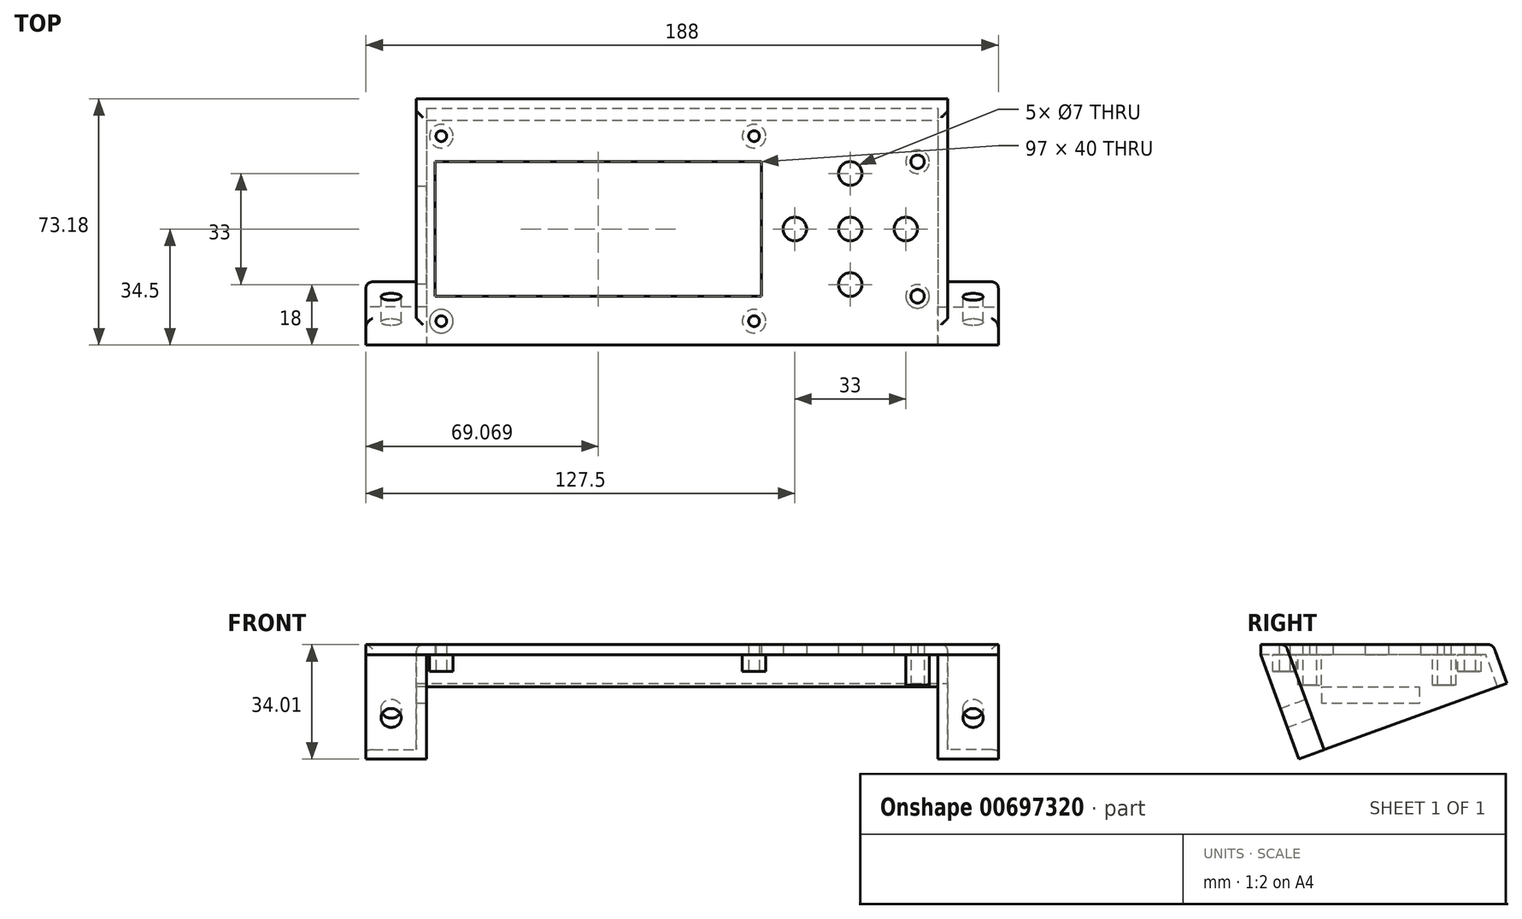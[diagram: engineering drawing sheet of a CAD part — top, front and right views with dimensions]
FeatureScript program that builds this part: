
annotation { "Feature Type Name" : "Feature", "Feature Type Description" : "" }
export const myFeature = defineFeature(function(context is Context, id is Id, definition is map)
    precondition{}
    {
        {
            var Q0;
            Q0=qCreatedBy(makeId("Top.planeOp"),FACE);
            var sketch = newSketch(context, id + "F0", { "sketchPlane" : qUnion([Q0])});
            skLineSegment(sketch, "E0.bottom", {"start": v(74, 29.5) * mm, "end": v(-74, 29.5) * mm});
            skLineSegment(sketch, "E0.top", {"start": v(74, -29.5) * mm, "end": v(-74, -29.5) * mm});
            skLineSegment(sketch, "E0.left", {"start": v(74, 29.5) * mm, "end": v(74, -29.5) * mm});
            skLineSegment(sketch, "E0.right", {"start": v(-74, 29.5) * mm, "end": v(-74, -29.5) * mm});
            skPoint(sketch, "E0.middle", {"position": v(0, 0) * mm});
            skCircle(sketch, "E1", {"center": v(30, 20) * mm, "radius": 2 * mm});
            skCircle(sketch, "E2.0.1.0", {"center": v(30, -20) * mm, "radius": 2 * mm});
            skCircle(sketch, "E2.1.0.0", {"center": v(70, 20) * mm, "radius": 2 * mm});
            skCircle(sketch, "E2.1.1.0", {"center": v(70, -20) * mm, "radius": 2 * mm});
            skLineSegment(sketch, "E2.direction1", {"start": v(30, 20) * mm, "end": v(70, 20) * mm, "construction": true});
            skLineSegment(sketch, "E2.direction2", {"start": v(30, 20) * mm, "end": v(30, -20) * mm, "construction": true});
            skCircle(sketch, "E3", {"center": v(-71.6, 27.6) * mm, "radius": 1.6 * mm});
            skCircle(sketch, "E4.0.1.0", {"center": v(-71.6, -27.4) * mm, "radius": 1.6 * mm});
            skCircle(sketch, "E4.1.0.0", {"center": v(21.4, 27.6) * mm, "radius": 1.6 * mm});
            skCircle(sketch, "E4.1.1.0", {"center": v(21.4, -27.4) * mm, "radius": 1.6 * mm});
            skLineSegment(sketch, "E4.direction1", {"start": v(-71.6, 27.6) * mm, "end": v(21.4, 27.6) * mm, "construction": true});
            skLineSegment(sketch, "E4.direction2", {"start": v(-71.6, 27.6) * mm, "end": v(-71.6, -27.4) * mm, "construction": true});
            skCircle(sketch, "E5", {"center": v(50, 0) * mm, "radius": 3.5 * mm});
            skCircle(sketch, "E6.1.0.0", {"center": v(66.5, 0) * mm, "radius": 3.5 * mm});
            skLineSegment(sketch, "E6.direction1", {"start": v(50, 0) * mm, "end": v(66.5, 0) * mm, "construction": true});
            skCircle(sketch, "E7.1.0.0", {"center": v(33.5, 0) * mm, "radius": 3.5 * mm});
            skLineSegment(sketch, "E7.direction1", {"start": v(50, 0) * mm, "end": v(33.5, 0) * mm, "construction": true});
            skCircle(sketch, "E8.0.1.0", {"center": v(50, 16.5) * mm, "radius": 3.5 * mm});
            skLineSegment(sketch, "E8.direction1", {"start": v(50, 0) * mm, "end": v(75.2, 0) * mm, "construction": true});
            skLineSegment(sketch, "E8.direction2", {"start": v(50, 0) * mm, "end": v(50, 16.5) * mm, "construction": true});
            skCircle(sketch, "E9.0.1.0", {"center": v(50, -16.5) * mm, "radius": 3.5 * mm});
            skLineSegment(sketch, "E9.direction2", {"start": v(50, 0) * mm, "end": v(50, -16.5) * mm, "construction": true});
            skLineSegment(sketch, "E10", {"start": v(21.4, -27.4) * mm, "end": v(-71.6, 27.6) * mm, "construction": true});
            skLineSegment(sketch, "E11", {"start": v(21.4, 27.6) * mm, "end": v(-71.6, -27.4) * mm, "construction": true});
            skPoint(sketch, "E12.middle", {"position": v(-24.93, 0) * mm});
            skLineSegment(sketch, "E13.bottom", {"start": v(23.57, 20) * mm, "end": v(-73.43, 20) * mm});
            skLineSegment(sketch, "E13.top", {"start": v(23.57, -20) * mm, "end": v(-73.43, -20) * mm});
            skLineSegment(sketch, "E13.left", {"start": v(23.57, 20) * mm, "end": v(23.57, -20) * mm});
            skLineSegment(sketch, "E13.right", {"start": v(-73.43, 20) * mm, "end": v(-73.43, -20) * mm});
            skSolve(sketch);
        }
        {
            var Q0;
            Q0=makeQuery(id+"F0.imprint","IMPRINT",FACE,{"disambiguationData":[TD([[makeQuery(id+"F0.imprint","IMPRINT",EDGE,{"derivedFrom":sQuery(id+"F0.wireOp",EDGE,"E0.bottom")}),1.0]])]});
            var Q1;
            Q1=makeQuery(id+"F0.imprint","IMPRINT",FACE,{"disambiguationData":[TD([[makeQuery(id+"F0.imprint","IMPRINT",EDGE,{"derivedFrom":sQuery(id+"F0.wireOp",EDGE,"E2.0.1.0")}),1.0]])]});
            var Q2;
            Q2=makeQuery(id+"F0.imprint","IMPRINT",FACE,{"disambiguationData":[TD([[makeQuery(id+"F0.imprint","IMPRINT",EDGE,{"derivedFrom":sQuery(id+"F0.wireOp",EDGE,"E1")}),1.0]])]});
            extrude(context, id + "F1", {"entities" : qUnion([Q0, Q1, Q2]), "depth" : 3 * mm, "offsetDistance" : 25 * mm});
        }
        {
            var Q0;
            Q0=makeQuery(id+"F1.opExtrude","CAP_FACE",FACE,{"disambiguationData":[OSD([sQuery(id+"F0.wireOp",EDGE,"E0.bottom"),sQuery(id+"F0.wireOp",EDGE,"E0.top"),sQuery(id+"F0.wireOp",EDGE,"E0.left"),sQuery(id+"F0.wireOp",EDGE,"E0.right"),sQuery(id+"F0.wireOp",EDGE,"E2.1.0.0"),sQuery(id+"F0.wireOp",EDGE,"E2.1.1.0"),sQuery(id+"F0.wireOp",EDGE,"E3"),sQuery(id+"F0.wireOp",EDGE,"E4.0.1.0"),sQuery(id+"F0.wireOp",EDGE,"E5"),sQuery(id+"F0.wireOp",EDGE,"E6.1.0.0"),sQuery(id+"F0.wireOp",EDGE,"E7.1.0.0"),sQuery(id+"F0.wireOp",EDGE,"E8.0.1.0"),sQuery(id+"F0.wireOp",EDGE,"E9.0.1.0"),sQuery(id+"F0.wireOp",EDGE,"E13.bottom"),sQuery(id+"F0.wireOp",EDGE,"E13.top"),sQuery(id+"F0.wireOp",EDGE,"E13.left"),sQuery(id+"F0.wireOp",EDGE,"E13.right")])],"isStart":true});
            var sketch = newSketch(context, id + "F2", { "sketchPlane" : qUnion([Q0])});
            skCircle(sketch, "E14", {"center": v(70, -20) * mm, "radius": 3.5 * mm});
            skCircle(sketch, "E15", {"center": v(70, 20) * mm, "radius": 3.5 * mm});
            skCircle(sketch, "E16", {"center": v(-71.6, -27.6) * mm, "radius": 3.5 * mm});
            skCircle(sketch, "E17", {"center": v(-71.6, 27.4) * mm, "radius": 3.5 * mm});
            skPoint(sketch, "E18.0", {"position": v(30, 20) * mm});
            skPoint(sketch, "E19.0", {"position": v(30, -20) * mm});
            skCircle(sketch, "E20.0", {"center": v(21.4, -27.6) * mm, "radius": 1.6 * mm});
            skCircle(sketch, "E20.1", {"center": v(21.4, 27.4) * mm, "radius": 1.6 * mm});
            skCircle(sketch, "E21", {"center": v(21.4, -27.6) * mm, "radius": 3.5 * mm});
            skCircle(sketch, "E22", {"center": v(21.4, 27.4) * mm, "radius": 3.5 * mm});
            skSolve(sketch);
        }
        {
            var Q0;
            Q0=makeQuery(id+"F2.imprint","IMPRINT",FACE,{"disambiguationData":[TD([[makeQuery(id+"F2.imprint","IMPRINT",EDGE,{"derivedFrom":sQuery(id+"F2.wireOp",EDGE,"E14")}),1.0]])]});
            var Q1;
            Q1=makeQuery(id+"F2.imprint","IMPRINT",FACE,{"disambiguationData":[TD([[makeQuery(id+"F2.imprint","IMPRINT",EDGE,{"derivedFrom":sQuery(id+"F2.wireOp",EDGE,"E15")}),1.0]])]});
            extrude(context, id + "F3", {"entities" : qUnion([Q0, Q1]), "operationType" : NewBodyOperationType.ADD, "depth" : 9 * mm, "offsetDistance" : 25 * mm});
        }
        {
            var Q0;
            Q0=makeQuery(id+"F2.imprint","IMPRINT",FACE,{"disambiguationData":[TD([[makeQuery(id+"F2.imprint","IMPRINT",EDGE,{"derivedFrom":makeQuery(id+"F1.opExtrude","CAP_EDGE",EDGE,{"disambiguationData":[OSD([sQuery(id+"F0.wireOp",EDGE,"E3")])],"isStart":true})}),1.0]])]});
            var Q1;
            {var subQ0=sQuery(id+"F2.wireOp",EDGE,"E16");var subQ1=makeQuery(id+"F1.opExtrude","CAP_EDGE",EDGE,{"disambiguationData":[OSD([sQuery(id+"F0.wireOp",EDGE,"E0.bottom")])],"isStart":true});var subQ2=makeQuery(id+"F2.imprint","INTERSECT",VERTEX,{"derivedFrom":[subQ1,subQ0]});Q1=makeQuery(id+"F2.imprint","IMPRINT",FACE,{"disambiguationData":[TD([[makeQuery(id+"F2.imprint","IMPRINT",EDGE,{"disambiguationData":[TD([[subQ2,1.0]])],"derivedFrom":subQ0}),1.0]])]});}
            var Q2;
            Q2=makeQuery(id+"F2.imprint","IMPRINT",FACE,{"disambiguationData":[TD([[makeQuery(id+"F2.imprint","IMPRINT",EDGE,{"derivedFrom":makeQuery(id+"F1.opExtrude","CAP_EDGE",EDGE,{"disambiguationData":[OSD([sQuery(id+"F0.wireOp",EDGE,"E4.0.1.0")])],"isStart":true})}),1.0]])]});
            var Q3;
            {var subQ0=sQuery(id+"F2.wireOp",EDGE,"E17");var subQ1=makeQuery(id+"F1.opExtrude","CAP_EDGE",EDGE,{"disambiguationData":[OSD([sQuery(id+"F0.wireOp",EDGE,"E0.top")])],"isStart":true});var subQ2=makeQuery(id+"F2.imprint","INTERSECT",VERTEX,{"derivedFrom":[subQ1,subQ0]});Q3=makeQuery(id+"F2.imprint","IMPRINT",FACE,{"disambiguationData":[TD([[makeQuery(id+"F2.imprint","IMPRINT",EDGE,{"disambiguationData":[TD([[subQ2,-1.0]])],"derivedFrom":subQ0}),1.0]])]});}
            var Q4;
            {var subQ0=sQuery(id+"F2.wireOp",EDGE,"E21");var subQ1=makeQuery(id+"F1.opExtrude","CAP_EDGE",EDGE,{"disambiguationData":[OSD([sQuery(id+"F0.wireOp",EDGE,"E0.bottom")])],"isStart":true});var subQ2=makeQuery(id+"F2.imprint","INTERSECT",VERTEX,{"disambiguationData":[OD(0.0)],"derivedFrom":[subQ1,subQ0]});Q4=makeQuery(id+"F2.imprint","IMPRINT",FACE,{"disambiguationData":[TD([[makeQuery(id+"F2.imprint","IMPRINT",EDGE,{"disambiguationData":[TD([[subQ2,1.0]])],"derivedFrom":subQ0}),1.0]])]});}
            var Q5;
            Q5=makeQuery(id+"F2.imprint","IMPRINT",FACE,{"disambiguationData":[TD([[makeQuery(id+"F2.imprint","IMPRINT",EDGE,{"derivedFrom":sQuery(id+"F2.wireOp",EDGE,"E20.0")}),1.0]])]});
            var Q6;
            Q6=makeQuery(id+"F2.imprint","IMPRINT",FACE,{"disambiguationData":[TD([[makeQuery(id+"F2.imprint","IMPRINT",EDGE,{"derivedFrom":sQuery(id+"F2.wireOp",EDGE,"E20.1")}),1.0]])]});
            var Q7;
            {var subQ0=sQuery(id+"F2.wireOp",EDGE,"E22");var subQ1=makeQuery(id+"F1.opExtrude","CAP_EDGE",EDGE,{"disambiguationData":[OSD([sQuery(id+"F0.wireOp",EDGE,"E0.top")])],"isStart":true});var subQ2=makeQuery(id+"F2.imprint","INTERSECT",VERTEX,{"disambiguationData":[OD(0.0)],"derivedFrom":[subQ1,subQ0]});Q7=makeQuery(id+"F2.imprint","IMPRINT",FACE,{"disambiguationData":[TD([[makeQuery(id+"F2.imprint","IMPRINT",EDGE,{"disambiguationData":[TD([[subQ2,-1.0]])],"derivedFrom":subQ0}),1.0]])]});}
            extrude(context, id + "F4", {"entities" : qUnion([Q0, Q1, Q2, Q3, Q4, Q5, Q6, Q7]), "operationType" : NewBodyOperationType.ADD, "depth" : 5 * mm, "offsetDistance" : 25 * mm});
        }
        {
            var Q0;
            Q0=makeQuery(id+"F1.opExtrude","SWEPT_FACE",FACE,{"disambiguationData":[OSD([sQuery(id+"F0.wireOp",EDGE,"E0.right")])]});
            extrude(context, id + "F5", {"entities" : qUnion([Q0]), "operationType" : NewBodyOperationType.ADD, "depth" : 5 * mm, "offsetDistance" : 25 * mm});
        }
        {
            var Q0;
            {var subQ0=sQuery(id+"F0.wireOp",EDGE,"E0.bottom");Q0=makeQuery(id+"F5.boolean.opBoolean","MERGE",FACE,{"derivedFrom":[makeQuery(id+"F1.opExtrude","SWEPT_FACE",FACE,{"disambiguationData":[OSD([subQ0])]}),makeQuery(id+"F5.opExtrude","SWEPT_FACE",FACE,{"disambiguationData":[OSD([subQ0,sQuery(id+"F0.wireOp",EDGE,"E0.right")])]})]});}
            extrude(context, id + "F6", {"entities" : qUnion([Q0]), "operationType" : NewBodyOperationType.ADD, "depth" : 5 * mm, "offsetDistance" : 25 * mm});
        }
        {
            var Q0;
            {var subQ0=sQuery(id+"F0.wireOp",EDGE,"E0.top");Q0=makeQuery(id+"F5.boolean.opBoolean","MERGE",FACE,{"derivedFrom":[makeQuery(id+"F1.opExtrude","SWEPT_FACE",FACE,{"disambiguationData":[OSD([subQ0])]}),makeQuery(id+"F5.opExtrude","SWEPT_FACE",FACE,{"disambiguationData":[OSD([subQ0,sQuery(id+"F0.wireOp",EDGE,"E0.right")])]})]});}
            extrude(context, id + "F7", {"entities" : qUnion([Q0]), "operationType" : NewBodyOperationType.ADD, "depth" : 5 * mm, "offsetDistance" : 25 * mm});
        }
        {
            var Q0;
            {var subQ0=sQuery(id+"F0.wireOp",EDGE,"E0.left");Q0=makeQuery(id+"F7.boolean.opBoolean","MERGE",FACE,{"derivedFrom":[makeQuery(id+"F6.boolean.opBoolean","MERGE",FACE,{"derivedFrom":[makeQuery(id+"F1.opExtrude","SWEPT_FACE",FACE,{"disambiguationData":[OSD([subQ0])]}),makeQuery(id+"F6.opExtrude","SWEPT_FACE",FACE,{"disambiguationData":[OSD([sQuery(id+"F0.wireOp",EDGE,"E0.bottom"),subQ0])]})]}),makeQuery(id+"F7.opExtrude","SWEPT_FACE",FACE,{"disambiguationData":[OSD([sQuery(id+"F0.wireOp",EDGE,"E0.top"),subQ0])]})]});}
            extrude(context, id + "F8", {"entities" : qUnion([Q0]), "operationType" : NewBodyOperationType.ADD, "depth" : 5 * mm, "offsetDistance" : 25 * mm});
        }
        {
            var Q0;
            Q0=makeQuery(id+"F8.opExtrude","CAP_FACE",FACE,{"disambiguationData":[OSD([sQuery(id+"F0.wireOp",EDGE,"E0.bottom"),sQuery(id+"F0.wireOp",EDGE,"E0.top"),sQuery(id+"F0.wireOp",EDGE,"E0.left")])],"isStart":false});
            var sketch = newSketch(context, id + "F9", { "sketchPlane" : qUnion([Q0])});
            skLineSegment(sketch, "E23", {"start": v(-34.5, 0) * mm, "end": v(-24.24, -28.2) * mm});
            skLineSegment(sketch, "E24", {"start": v(34.5, 3) * mm, "end": v(37.65, -5.66) * mm});
            skLineSegment(sketch, "E25", {"start": v(37.65, -5.66) * mm, "end": v(-24.24, -28.2) * mm});
            skSolve(sketch);
        }
        {
            var Q0;
            Q0 = qSketchRegion(id + "F9", true);
            var Q1;
            Q1=makeQuery(id+"F9.imprint","IMPRINT",FACE,{"disambiguationData":[TD([[makeQuery(id+"F9.imprint","IMPRINT",EDGE,{"derivedFrom":sQuery(id+"F9.wireOp",EDGE,"E23")}),1.0]])]});
            extrude(context, id + "F10", {"entities" : qUnion([Q0, Q1]), "operationType" : NewBodyOperationType.ADD, "oppositeDirection" : true, "depth" : 3 * mm, "offsetDistance" : 25 * mm});
        }
        {
            var Q0;
            {var subQ0=sQuery(id+"F0.wireOp",EDGE,"E0.right");var subQ1=sQuery(id+"F0.wireOp",EDGE,"E0.top");var subQ2=sQuery(id+"F0.wireOp",EDGE,"E0.bottom");Q0=makeQuery(id+"F7.boolean.opBoolean","MERGE",FACE,{"derivedFrom":[makeQuery(id+"F6.boolean.opBoolean","MERGE",FACE,{"derivedFrom":[makeQuery(id+"F5.opExtrude","CAP_FACE",FACE,{"disambiguationData":[OSD([subQ0])],"isStart":false}),makeQuery(id+"F6.opExtrude","SWEPT_FACE",FACE,{"disambiguationData":[OSD([subQ2,subQ0]),TDD([makeQuery(id+"F5.opExtrude","CAP_EDGE",EDGE,{"disambiguationData":[OSD([subQ2,subQ0])],"isStart":false})])]})]}),makeQuery(id+"F7.opExtrude","SWEPT_FACE",FACE,{"disambiguationData":[OSD([subQ1,subQ0]),TDD([makeQuery(id+"F5.opExtrude","CAP_EDGE",EDGE,{"disambiguationData":[OSD([subQ1,subQ0])],"isStart":false})])]})]});}
            var sketch = newSketch(context, id + "F11", { "sketchPlane" : qUnion([Q0])});
            skLineSegment(sketch, "E26.1.0", {"start": v(-34.5, 3) * mm, "end": v(-37.65, -5.66) * mm});
            skLineSegment(sketch, "E26.1.1", {"start": v(-37.65, -5.66) * mm, "end": v(24.24, -28.2) * mm});
            skLineSegment(sketch, "E26.1.2", {"start": v(24.24, -28.2) * mm, "end": v(34.5, 0) * mm});
            skLineSegment(sketch, "E26.1.3", {"start": v(34.5, 0) * mm, "end": v(-34.5, 0) * mm});
            skLineSegment(sketch, "E26.1.4", {"start": v(-34.5, 0) * mm, "end": v(-34.5, 3) * mm});
            skLineSegment(sketch, "E27.0", {"start": v(16.4, -9.5) * mm, "end": v(-12.6, -9.5) * mm});
            skLineSegment(sketch, "E28", {"start": v(-12.6, -9.5) * mm, "end": v(-12.6, -14.5) * mm});
            skLineSegment(sketch, "E29", {"start": v(-27.6, -9.32) * mm, "end": v(-27.6, -9.5) * mm});
            skLineSegment(sketch, "E30", {"start": v(-12.6, -14.5) * mm, "end": v(16.4, -14.5) * mm});
            skLineSegment(sketch, "E31", {"start": v(16.4, -14.5) * mm, "end": v(16.4, -9.5) * mm});
            skLineSegment(sketch, "E32.trimOffspring", {"start": v(-27.11, -9.5) * mm, "end": v(-27.6, -9.5) * mm});
            skSolve(sketch);
        }
        {
            var Q0;
            Q0=makeQuery(id+"F11.imprint","IMPRINT",FACE,{"disambiguationData":[TD([[makeQuery(id+"F11.imprint","IMPRINT",EDGE,{"derivedFrom":sQuery(id+"F11.wireOp",EDGE,"E26.1.0")}),1.0]])]});
            extrude(context, id + "F12", {"entities" : qUnion([Q0]), "operationType" : NewBodyOperationType.ADD, "oppositeDirection" : true, "depth" : 3 * mm, "offsetDistance" : 25 * mm});
        }
        {
            var Q0;
            Q0=makeQuery(id+"F10.opExtrude","CAP_FACE",FACE,{"disambiguationData":[OSD([sQuery(id+"F0.wireOp",EDGE,"E0.bottom"),sQuery(id+"F0.wireOp",EDGE,"E0.top"),sQuery(id+"F0.wireOp",EDGE,"E0.left"),sQuery(id+"F9.wireOp",EDGE,"E23"),sQuery(id+"F9.wireOp",EDGE,"E24"),sQuery(id+"F9.wireOp",EDGE,"E25")])],"isStart":false});
            var sketch = newSketch(context, id + "F13", { "sketchPlane" : qUnion([Q0])});
            skLineSegment(sketch, "E33", {"start": v(-34.83, -6.69) * mm, "end": v(-32.4, 0) * mm});
            skSolve(sketch);
        }
        {
            var Q0;
            Q0 = qSketchRegion(id + "F13", true);
            var Q1;
            {var subQ5=sQuery(id+"F13.wireOp",EDGE,"E33");Q1=makeQuery(id+"F13.imprint","IMPRINT",FACE,{"disambiguationData":[TD([[makeQuery(id+"F13.imprint","IMPRINT",EDGE,{"derivedFrom":subQ5}),1.0]])]});}
            extrude(context, id + "F14", {"entities" : qUnion([Q0, Q1]), "operationType" : NewBodyOperationType.ADD, "endBound" : BoundingType.UP_TO_NEXT, "depth" : 122 * mm, "offsetDistance" : 25 * mm});
        }
        {
            var Q0;
            {var subQ0=sQuery(id+"F0.wireOp",EDGE,"E0.right");var subQ1=sQuery(id+"F0.wireOp",EDGE,"E0.top");var subQ2=sQuery(id+"F0.wireOp",EDGE,"E0.bottom");Q0=makeQuery(id+"F12.boolean.opBoolean","MERGE",FACE,{"derivedFrom":[makeQuery(id+"F7.boolean.opBoolean","MERGE",FACE,{"derivedFrom":[makeQuery(id+"F6.boolean.opBoolean","MERGE",FACE,{"derivedFrom":[makeQuery(id+"F5.opExtrude","CAP_FACE",FACE,{"disambiguationData":[OSD([subQ0])],"isStart":false}),makeQuery(id+"F6.opExtrude","SWEPT_FACE",FACE,{"disambiguationData":[OSD([subQ2,subQ0]),TDD([makeQuery(id+"F5.opExtrude","CAP_EDGE",EDGE,{"disambiguationData":[OSD([subQ2,subQ0])],"isStart":false})])]})]}),makeQuery(id+"F7.opExtrude","SWEPT_FACE",FACE,{"disambiguationData":[OSD([subQ1,subQ0]),TDD([makeQuery(id+"F5.opExtrude","CAP_EDGE",EDGE,{"disambiguationData":[OSD([subQ1,subQ0])],"isStart":false})])]})]}),makeQuery(id+"F12.opExtrude","CAP_FACE",FACE,{"disambiguationData":[OSD([sQuery(id+"F11.wireOp",EDGE,"E26.1.0"),sQuery(id+"F11.wireOp",EDGE,"E26.1.1"),sQuery(id+"F11.wireOp",EDGE,"E26.1.2"),sQuery(id+"F11.wireOp",EDGE,"E26.1.3"),sQuery(id+"F11.wireOp",EDGE,"E26.1.4")])],"isStart":true})]});}
            var sketch = newSketch(context, id + "F15", { "sketchPlane" : qUnion([Q0])});
            skLineSegment(sketch, "E34", {"start": v(16.72, -25.45) * mm, "end": v(27.08, 3) * mm});
            skSolve(sketch);
        }
        {
            var Q0;
            {var subQ0=sQuery(id+"F0.wireOp",EDGE,"E0.left");var subQ1=sQuery(id+"F0.wireOp",EDGE,"E0.top");var subQ2=sQuery(id+"F0.wireOp",EDGE,"E0.bottom");Q0=makeQuery(id+"F10.boolean.opBoolean","MERGE",FACE,{"derivedFrom":[makeQuery(id+"F8.opExtrude","CAP_FACE",FACE,{"disambiguationData":[OSD([subQ2,subQ1,subQ0])],"isStart":false}),makeQuery(id+"F10.opExtrude","CAP_FACE",FACE,{"disambiguationData":[OSD([subQ2,subQ1,subQ0,sQuery(id+"F9.wireOp",EDGE,"E23"),sQuery(id+"F9.wireOp",EDGE,"E24"),sQuery(id+"F9.wireOp",EDGE,"E25")])],"isStart":true})]});}
            var sketch = newSketch(context, id + "F16", { "sketchPlane" : qUnion([Q0])});
            skLineSegment(sketch, "E35", {"start": v(-16.72, -25.45) * mm, "end": v(-27.08, 3) * mm});
            skSolve(sketch);
        }
        {
            var Q0;
            Q0 = qSketchRegion(id + "F16", true);
            var Q1;
            {var subQ5=sQuery(id+"F16.wireOp",EDGE,"E35");Q1=makeQuery(id+"F16.imprint","IMPRINT",FACE,{"disambiguationData":[TD([[makeQuery(id+"F16.imprint","IMPRINT",EDGE,{"derivedFrom":subQ5}),1.0]])]});}
            extrude(context, id + "F17", {"entities" : qUnion([Q0, Q1]), "operationType" : NewBodyOperationType.ADD, "depth" : 15 * mm, "offsetDistance" : 25 * mm});
        }
        {
            var Q0;
            Q0 = qSketchRegion(id + "F15", true);
            var Q1;
            {var subQ5=sQuery(id+"F15.wireOp",EDGE,"E34");Q1=makeQuery(id+"F15.imprint","IMPRINT",FACE,{"disambiguationData":[TD([[makeQuery(id+"F15.imprint","IMPRINT",EDGE,{"derivedFrom":subQ5}),-1.0]])]});}
            extrude(context, id + "F18", {"entities" : qUnion([Q0, Q1]), "operationType" : NewBodyOperationType.ADD, "depth" : 15 * mm, "offsetDistance" : 25 * mm});
        }
        {
            var Q0;
            Q0=makeQuery(id+"F18.opExtrude","SWEPT_FACE",FACE,{"disambiguationData":[OSD([sQuery(id+"F15.wireOp",EDGE,"E34")])]});
            var sketch = newSketch(context, id + "F19", { "sketchPlane" : qUnion([Q0])});
            skCircle(sketch, "E36", {"center": v(86.5, -8.2) * mm, "radius": 3 * mm});
            skCircle(sketch, "E37", {"center": v(-86.5, -8.2) * mm, "radius": 3 * mm});
            skSolve(sketch);
        }
        {
            var Q0;
            Q0=makeQuery(id+"F19.imprint","IMPRINT",FACE,{"disambiguationData":[TD([[makeQuery(id+"F19.imprint","IMPRINT",EDGE,{"derivedFrom":sQuery(id+"F19.wireOp",EDGE,"E36")}),1.0]])]});
            var Q1;
            Q1=makeQuery(id+"F19.imprint","IMPRINT",FACE,{"disambiguationData":[TD([[makeQuery(id+"F19.imprint","IMPRINT",EDGE,{"derivedFrom":sQuery(id+"F19.wireOp",EDGE,"E37")}),1.0]])]});
            extrude(context, id + "F20", {"entities" : qUnion([Q0, Q1]), "operationType" : NewBodyOperationType.REMOVE, "oppositeDirection" : true, "depth" : 25 * mm, "offsetDistance" : 25 * mm});
        }
        {
            var Q0;
            {var subQ0=sQuery(id+"F9.wireOp",EDGE,"E24");var subQ1=sQuery(id+"F0.wireOp",EDGE,"E0.left");var subQ2=sQuery(id+"F0.wireOp",EDGE,"E0.top");var subQ3=sQuery(id+"F0.wireOp",EDGE,"E0.bottom");var subQ4=sQuery(id+"F0.wireOp",EDGE,"E0.right");var subQ5=makeQuery(id+"F8.boolean.opBoolean","MERGE",EDGE,{"derivedFrom":[makeQuery(id+"F6.opExtrude","CAP_EDGE",EDGE,{"disambiguationData":[OSD([subQ3,subQ4]),TDD([makeQuery(id+"F5.boolean.opBoolean","MERGE",EDGE,{"derivedFrom":[makeQuery(id+"F1.opExtrude","CAP_EDGE",EDGE,{"disambiguationData":[OSD([subQ3])],"isStart":false}),makeQuery(id+"F5.opExtrude","SWEPT_EDGE",EDGE,{"disambiguationData":[OSD([subQ3,subQ4]),TDD([makeQuery(id+"F1.opExtrude","CAP_VERTEX",VERTEX,{"disambiguationData":[OSD([subQ3,subQ4])],"isStart":false})])]})]})])],"isStart":false}),makeQuery(id+"F8.opExtrude","SWEPT_EDGE",EDGE,{"disambiguationData":[OSD([subQ3,subQ1]),TDD([makeQuery(id+"F6.opExtrude","CAP_VERTEX",VERTEX,{"disambiguationData":[OSD([subQ3,subQ1]),TDD([makeQuery(id+"F1.opExtrude","CAP_VERTEX",VERTEX,{"disambiguationData":[OSD([subQ3,subQ1])],"isStart":false})])],"isStart":false})])]})]});var subQ6=makeQuery(id+"F10.boolean.opBoolean","SPLIT",EDGE,{"derivedFrom":subQ5});Q0=makeQuery(id+"F14.boolean.opBoolean","MERGE",EDGE,{"derivedFrom":[makeQuery(id+"F10.boolean.opBoolean","MERGE",EDGE,{"derivedFrom":[subQ5,makeQuery(id+"F10.opExtrude","SWEPT_EDGE",EDGE,{"disambiguationData":[OSD([subQ3,subQ2,subQ1,subQ0])]})]}),makeQuery(id+"F12.boolean.opBoolean","MERGE",EDGE,{"derivedFrom":[subQ6,makeQuery(id+"F12.opExtrude","SWEPT_EDGE",EDGE,{"disambiguationData":[OSD([subQ3,subQ2,subQ4,sQuery(id+"F11.wireOp",EDGE,"E26.1.0"),sQuery(id+"F11.wireOp",EDGE,"E26.1.4")])]})]}),makeQuery(id+"F12.boolean.opBoolean","SPLIT",EDGE,{"derivedFrom":subQ6}),makeQuery(id+"F14.opExtrude","SWEPT_EDGE",EDGE,{"disambiguationData":[OSD([subQ3,subQ2,subQ1,subQ0])]})]});}
            var Q1;
            {var subQ0=sQuery(id+"F0.wireOp",EDGE,"E0.left");var subQ1=sQuery(id+"F0.wireOp",EDGE,"E0.top");var subQ2=sQuery(id+"F0.wireOp",EDGE,"E0.bottom");Q1=makeQuery(id+"F8.opExtrude","CAP_EDGE",EDGE,{"disambiguationData":[OSD([subQ2,subQ1,subQ0]),TDD([makeQuery(id+"F7.boolean.opBoolean","MERGE",EDGE,{"derivedFrom":[makeQuery(id+"F6.boolean.opBoolean","MERGE",EDGE,{"derivedFrom":[makeQuery(id+"F1.opExtrude","CAP_EDGE",EDGE,{"disambiguationData":[OSD([subQ0])],"isStart":false}),makeQuery(id+"F6.opExtrude","SWEPT_EDGE",EDGE,{"disambiguationData":[OSD([subQ2,subQ0]),TDD([makeQuery(id+"F1.opExtrude","CAP_VERTEX",VERTEX,{"disambiguationData":[OSD([subQ2,subQ0])],"isStart":false})])]})]}),makeQuery(id+"F7.opExtrude","SWEPT_EDGE",EDGE,{"disambiguationData":[OSD([subQ1,subQ0]),TDD([makeQuery(id+"F1.opExtrude","CAP_VERTEX",VERTEX,{"disambiguationData":[OSD([subQ1,subQ0])],"isStart":false})])]})]})])],"isStart":false});}
            var Q2;
            {var subQ0=sQuery(id+"F0.wireOp",EDGE,"E0.right");var subQ1=sQuery(id+"F0.wireOp",EDGE,"E0.top");var subQ2=sQuery(id+"F0.wireOp",EDGE,"E0.bottom");Q2=makeQuery(id+"F7.boolean.opBoolean","MERGE",EDGE,{"derivedFrom":[makeQuery(id+"F6.boolean.opBoolean","MERGE",EDGE,{"derivedFrom":[makeQuery(id+"F5.opExtrude","CAP_EDGE",EDGE,{"disambiguationData":[OSD([subQ0]),TDD([makeQuery(id+"F1.opExtrude","CAP_EDGE",EDGE,{"disambiguationData":[OSD([subQ0])],"isStart":false})])],"isStart":false}),makeQuery(id+"F6.opExtrude","SWEPT_EDGE",EDGE,{"disambiguationData":[OSD([subQ2,subQ0]),TDD([makeQuery(id+"F5.opExtrude","CAP_VERTEX",VERTEX,{"disambiguationData":[OSD([subQ2,subQ0]),TDD([makeQuery(id+"F1.opExtrude","CAP_VERTEX",VERTEX,{"disambiguationData":[OSD([subQ2,subQ0])],"isStart":false})])],"isStart":false})])]})]}),makeQuery(id+"F7.opExtrude","SWEPT_EDGE",EDGE,{"disambiguationData":[OSD([subQ1,subQ0]),TDD([makeQuery(id+"F5.opExtrude","CAP_VERTEX",VERTEX,{"disambiguationData":[OSD([subQ1,subQ0]),TDD([makeQuery(id+"F1.opExtrude","CAP_VERTEX",VERTEX,{"disambiguationData":[OSD([subQ1,subQ0])],"isStart":false})])],"isStart":false})])]})]});}
            var Q3;
            Q3=makeQuery(id+"F18.opExtrude","SWEPT_EDGE",EDGE,{"disambiguationData":[OSD([sQuery(id+"F0.wireOp",EDGE,"E0.bottom"),sQuery(id+"F0.wireOp",EDGE,"E0.top"),sQuery(id+"F0.wireOp",EDGE,"E0.right"),sQuery(id+"F15.wireOp",EDGE,"E34")])]});
            var Q4;
            Q4=makeQuery(id+"F17.opExtrude","SWEPT_EDGE",EDGE,{"disambiguationData":[OSD([sQuery(id+"F0.wireOp",EDGE,"E0.bottom"),sQuery(id+"F0.wireOp",EDGE,"E0.top"),sQuery(id+"F0.wireOp",EDGE,"E0.left"),sQuery(id+"F16.wireOp",EDGE,"E35")])]});
            var Q5;
            Q5=makeQuery(id+"F17.opExtrude","CAP_EDGE",EDGE,{"disambiguationData":[OSD([sQuery(id+"F16.wireOp",EDGE,"E35")])],"isStart":false});
            var Q6;
            Q6=makeQuery(id+"F18.opExtrude","CAP_EDGE",EDGE,{"disambiguationData":[OSD([sQuery(id+"F15.wireOp",EDGE,"E34")])],"isStart":false});
            fillet(context, id + "F21", {"entities" : qUnion([Q0, Q1, Q2, Q3, Q4, Q5, Q6]), "radius" : 2 * mm, "tangentPropagation" : true, "allowEdgeOverflow" : false});
        }
        {
            var Q0;
            {var subQ0=sQuery(id+"F11.wireOp",EDGE,"E26.1.1");var subQ1=sQuery(id+"F9.wireOp",EDGE,"E25");Q0=makeQuery(id+"F18.boolean.opBoolean","MERGE",FACE,{"derivedFrom":[makeQuery(id+"F17.boolean.opBoolean","MERGE",FACE,{"derivedFrom":[makeQuery(id+"F14.boolean.opBoolean","MERGE",FACE,{"derivedFrom":[makeQuery(id+"F10.opExtrude","SWEPT_FACE",FACE,{"disambiguationData":[OSD([subQ1])]}),makeQuery(id+"F12.opExtrude","SWEPT_FACE",FACE,{"disambiguationData":[OSD([subQ0])]}),makeQuery(id+"F14.opExtrude","SWEPT_FACE",FACE,{"disambiguationData":[OSD([subQ1])]})]}),makeQuery(id+"F17.opExtrude","SWEPT_FACE",FACE,{"disambiguationData":[OSD([subQ1])]})]}),makeQuery(id+"F18.opExtrude","SWEPT_FACE",FACE,{"disambiguationData":[OSD([subQ0])]})]});}
            extrude(context, id + "F22", {"entities" : qUnion([Q0]), "operationType" : NewBodyOperationType.ADD, "depth" : 3 * mm, "offsetDistance" : 25 * mm});
        }
        {
            var Q0;
            Q0=makeQuery(id+"F12.opExtrude","SWEPT_FACE",FACE,{"disambiguationData":[OSD([sQuery(id+"F11.wireOp",EDGE,"E30")])]});
            extrude(context, id + "F23", {"entities" : qUnion([Q0]), "operationType" : NewBodyOperationType.ADD, "oppositeDirection" : true, "depth" : 1.5 * mm, "offsetDistance" : 25 * mm});
        }
    });
